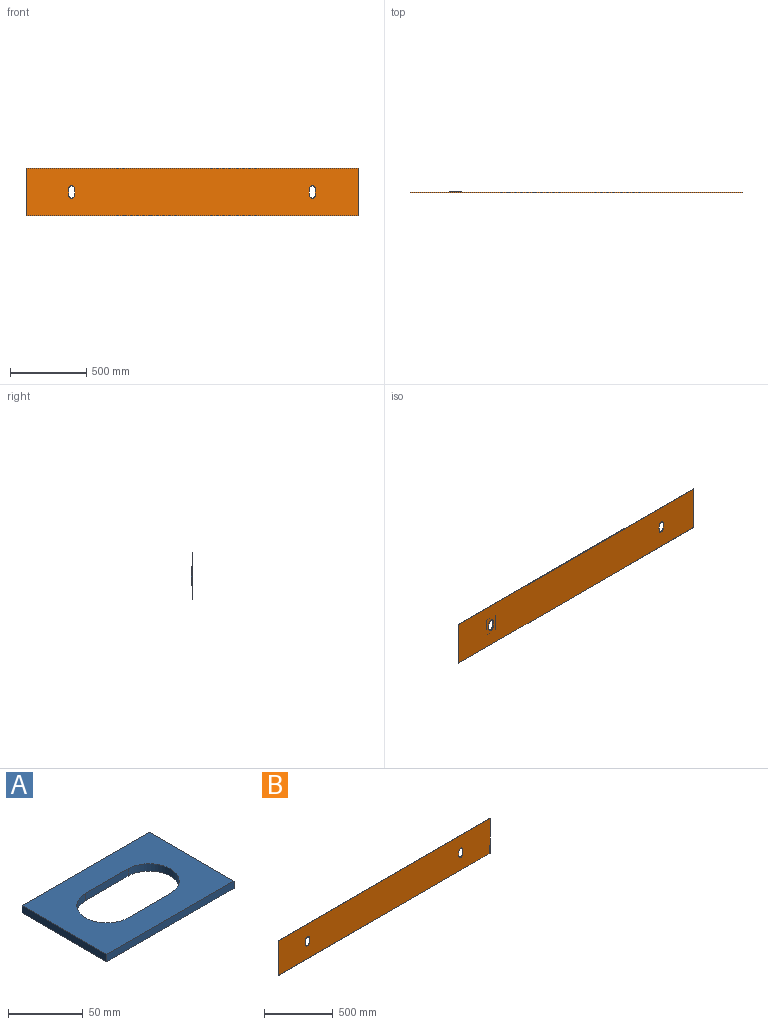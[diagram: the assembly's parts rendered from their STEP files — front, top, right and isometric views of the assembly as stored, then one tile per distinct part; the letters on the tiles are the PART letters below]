
ASSEMBLY  parts=2 mates=1
PART A: 10 faces, bbox 120x80x6 mm
  f0: plane 40x6mm, normal (0,-1,0), area 240mm2, adj f1,f7,f8,f9
  f1: cylinder r=20mm len=40mm, axis (0,0,-1), area 377mm2, adj f0,f2,f8,f9
  f2: plane 40x6mm, normal (0,1,0), area 240mm2, adj f1,f7,f8,f9
  f3: plane 80x6mm, normal (-1,0,0), area 480mm2, adj f4,f6,f8,f9
  f4: plane 120x6mm, normal (0,1,0), area 720mm2, adj f3,f5,f8,f9
  f5: plane 80x6mm, normal (1,0,0), area 480mm2, adj f4,f6,f8,f9
  f6: plane 120x6mm, normal (0,-1,0), area 720mm2, adj f3,f5,f8,f9
  f7: cylinder r=20mm len=40mm, axis (0,0,-1), area 377mm2, adj f0,f2,f8,f9
  f8: plane 120x80mm, normal (0,0,-1), area 6743.4mm2, adj f0,f1,f2,f3,f4,f5,f6,f7
  f9: plane 120x80mm, normal (0,0,1), area 6743.4mm2, adj f0,f1,f2,f3,f4,f5,f6,f7
PART B: 14 faces, bbox 2180x3x310 mm
  f0: plane 310x3mm, normal (-1,0,0), area 930mm2, adj f1,f11,f12,f13
  f1: plane 2180x3mm, normal (0,0,1), area 6540mm2, adj f0,f2,f12,f13
  f2: plane 310x3mm, normal (1,0,0), area 930mm2, adj f1,f11,f12,f13
  f3: cylinder r=20mm len=40mm, axis (0,1,0), area 188.5mm2, adj f4,f10,f12,f13
  f4: plane 40x3mm, normal (-1,0,0), area 120mm2, adj f3,f5,f12,f13
  f5: cylinder r=20mm len=40mm, axis (0,1,0), area 188.5mm2, adj f4,f10,f12,f13
  f6: plane 40x3mm, normal (1,0,0), area 120mm2, adj f7,f9,f12,f13
  f7: cylinder r=20mm len=40mm, axis (0,1,0), area 188.5mm2, adj f6,f8,f12,f13
  f8: plane 40x3mm, normal (-1,0,0), area 120mm2, adj f7,f9,f12,f13
  f9: cylinder r=20mm len=40mm, axis (0,1,0), area 188.5mm2, adj f6,f8,f12,f13
  f10: plane 40x3mm, normal (1,0,0), area 120mm2, adj f3,f5,f12,f13
  f11: plane 2180x3mm, normal (0,0,-1), area 6540mm2, adj f0,f2,f12,f13
  f12: plane 2180x310mm, normal (0,1,0), area 670086.7mm2, adj f0,f1,f2,f3,f4,f5,f6,f7
  f13: plane 2180x310mm, normal (0,-1,0), area 670086.7mm2, adj f0,f1,f2,f3,f4,f5,f6,f7
PLACE A rot(axis=(-0.58,0.58,0.58),120deg) t=(-866.29,8.6,49.77)mm
PLACE B t=(-1206.29,-0.4,-165.23)mm
MATE fastened A.f8 <-> B.f12  axis (0,-1,0) through (-906.29,2.6,-10.23)mm
